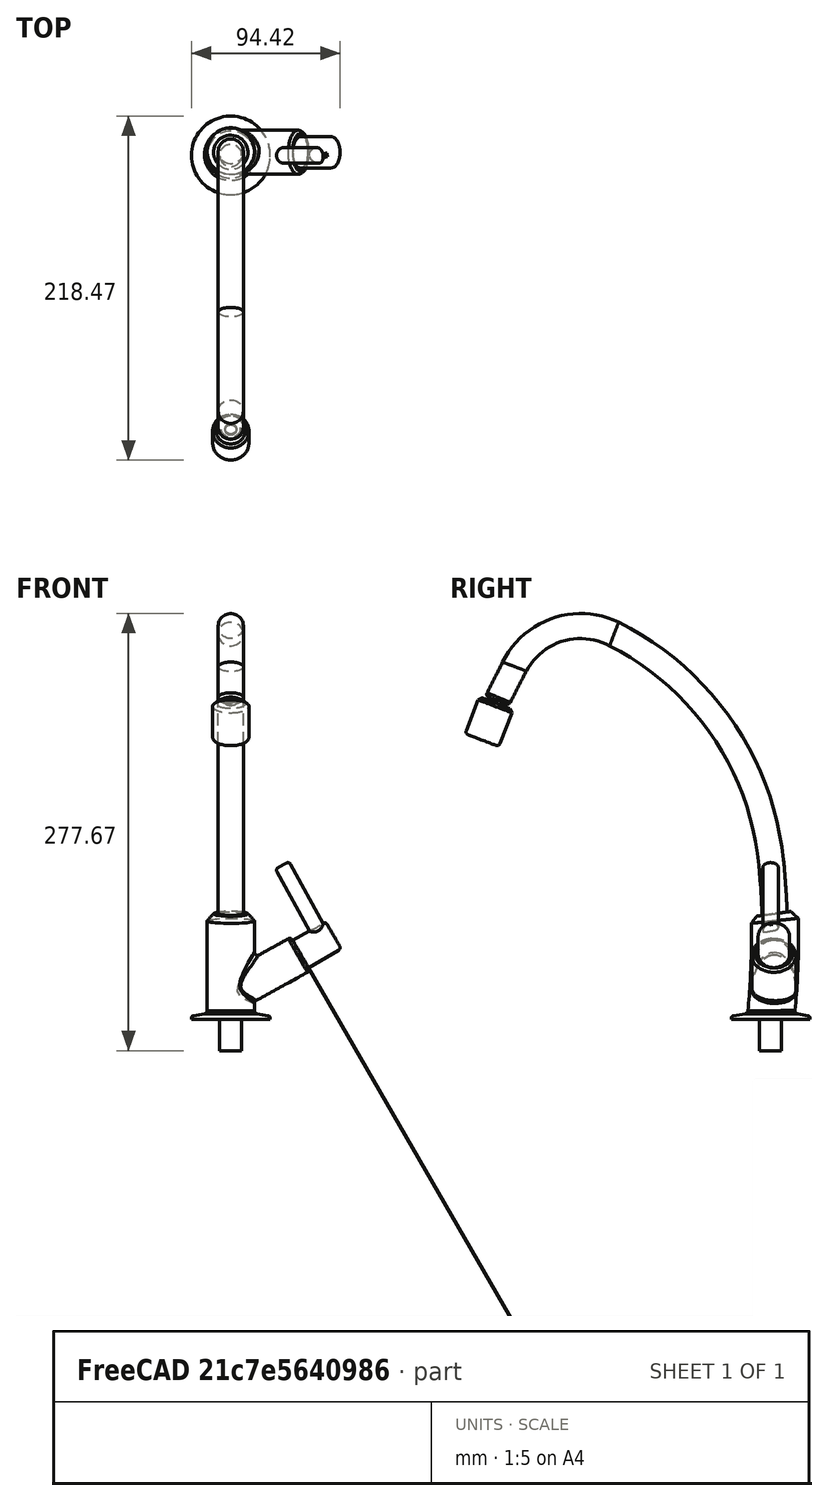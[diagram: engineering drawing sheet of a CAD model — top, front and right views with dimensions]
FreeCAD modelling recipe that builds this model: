
FCSTD DOCUMENT  (FreeCAD 1.0R38641 +468 (Git))
Label: Faucet_Lorenzetti_Cozinha
License: All rights reserved
objects: Part::Feature×1, Part::FeaturePython×1
note: 2 computed .brp shape members not serialized (recipe doc carries the construction recipe); baked Part::Feature solids carry a one-line shape summary decoded from their .brp

FEATURE [Part::Feature] Solid  label="Faucet_Lorenzetti_Cozinha"
  Placement = pos=(0,0,0) rot=(0.57735,0.57735,0.57735;2.0944rad)
  shape: bbox 96.81 x 221.3 x 295.3 mm, 58 faces (baked)
FEATURE [Part::FeaturePython] Component  label="Faucet_Lorenzetti_Cozinha001"  # Arch/BIM 22 (typed FeaturePython)
  Base = -> Solid
  HorizontalArea = 0
  IfcData = attributes={"GlobalId": {"name": "GlobalId", "type": "IfcGloballyUniqueId", "is_enum": false, "enum_values": []}, "Description": {"... (+538 chars omitted),+1 more (map truncated)
  IfcType = 22
  MoveBase = false
  MoveWithHost = false
  PerimeterLength = 0
  Placement = pos=(0,0,0) rot=(0.57735,0.57735,0.57735;2.0944rad)
  VerticalArea = 0
